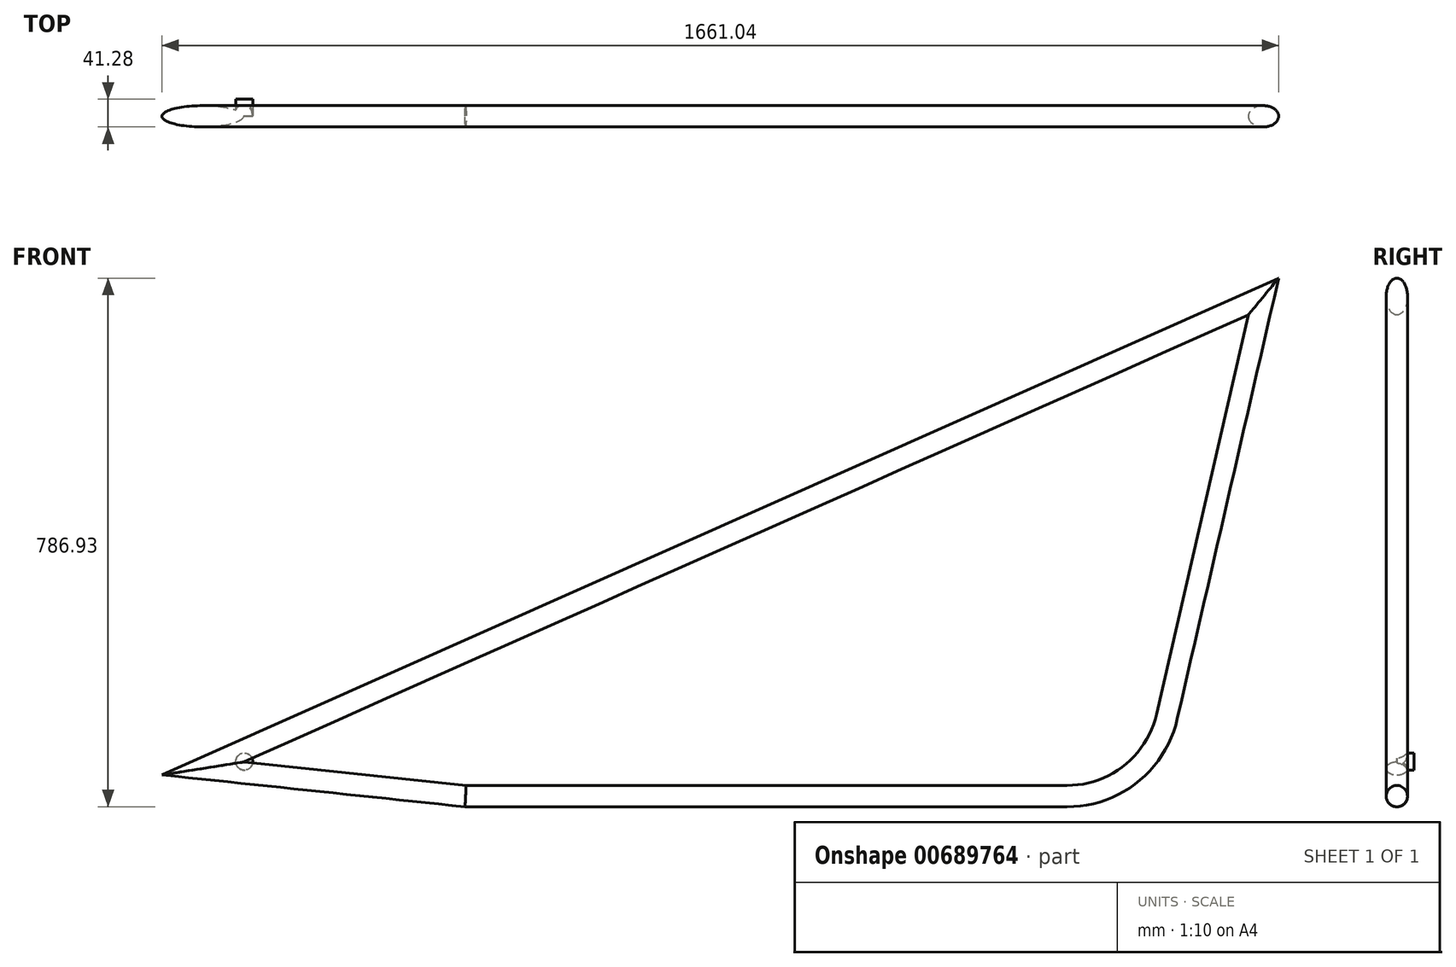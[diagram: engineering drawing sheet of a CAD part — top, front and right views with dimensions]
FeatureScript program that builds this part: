
annotation { "Feature Type Name" : "Feature", "Feature Type Description" : "" }
export const myFeature = defineFeature(function(context is Context, id is Id, definition is map)
    precondition{}
    {
        {
            var Q0;
            Q0=qCreatedBy(makeId("Front.planeOp"),FACE);
            var sketch = newSketch(context, id + "F0", { "sketchPlane" : qUnion([Q0])});
            skLineSegment(sketch, "E0", {"start": v(842.45, 702.52) * mm, "end": v(-735.42, 0) * mm});
            skLineSegment(sketch, "E1", {"start": v(-735.42, 0) * mm, "end": v(-344.34, -41.1) * mm});
            skLineSegment(sketch, "E2", {"start": v(-344.34, -41.1) * mm, "end": v(550.3, -41.1) * mm});
            skLineSegment(sketch, "E3", {"start": v(842.45, 702.52) * mm, "end": v(698.83, 77.18) * mm});
            skPoint(sketch, "E4.visualSharp", {"position": v(671.66, -41.1) * mm});
            skArc(sketch, "E4.filletArc", {"start": v(550.3, -41.1) * mm, "mid": v(645.23, -7.92) * mm, "end": v(698.83, 77.18) * mm});
            skLineSegment(sketch, "E5", {"start": v(-29.69, 314.21) * mm, "end": v(-29.69, -41.1) * mm});
            skLineSegment(sketch, "E6", {"start": v(-735.42, 0) * mm, "end": v(-539.88, -20.55) * mm});
            skLineSegment(sketch, "E7", {"start": v(-735.42, 0) * mm, "end": v(1316.3, 0) * mm});
            skLineSegment(sketch, "E8", {"start": v(842.45, 702.52) * mm, "end": v(842.45, -98.36) * mm});
            skLineSegment(sketch, "E9", {"start": v(842.45, 702.52) * mm, "end": v(1316.3, 0) * mm});
            skSolve(sketch);
        }
        {
            var Q0;
            Q0=qCreatedBy(makeId("Right.planeOp"),FACE);
            var sketch = newSketch(context, id + "F1", { "sketchPlane" : qUnion([Q0])});
            skCircle(sketch, "E10", {"center": v(0, -41.1) * mm, "radius": 15.88 * mm});
            skLineSegment(sketch, "E11", {"start": v(20.8, -41.41) * mm, "end": v(0, 154.77) * mm});
            skSolve(sketch);
        }
        {
            var Q0;
            Q0=makeQuery(id+"F1.imprint","IMPRINT",FACE,{"disambiguationData":[TD([[makeQuery(id+"F1.imprint","IMPRINT",EDGE,{"derivedFrom":sQuery(id+"F1.wireOp",EDGE,"E10")}),1.0]])]});
            var Q1;
            Q1=sQuery(id+"F0.wireOp",EDGE,"E2");
            var Q2;
            Q2=sQuery(id+"F0.wireOp",EDGE,"E4.filletArc");
            var Q3;
            Q3=sQuery(id+"F0.wireOp",EDGE,"E3");
            var Q4;
            Q4=sQuery(id+"F0.wireOp",EDGE,"E1");
            var Q5;
            Q5=sQuery(id+"F0.wireOp",EDGE,"E0");
            sweep(context, id + "F2", {"profiles" : qUnion([Q0]), "path" : qUnion([Q1, Q2, Q3, Q4, Q5])});
        }
        {
            var Q0;
            Q0=qCreatedBy(makeId("Front.planeOp"),FACE);
            var sketch = newSketch(context, id + "F3", { "sketchPlane" : qUnion([Q0])});
            skCircle(sketch, "E12", {"center": v(-673.59, 10.26) * mm, "radius": 12.7 * mm});
            skSolve(sketch);
        }
        {
            var Q0;
            Q0=makeQuery(id+"F3.imprint","IMPRINT",FACE,{"disambiguationData":[TD([[makeQuery(id+"F3.imprint","IMPRINT",EDGE,{"derivedFrom":sQuery(id+"F3.wireOp",EDGE,"E12")}),1.0]])]});
            extrude(context, id + "F4", {"entities" : qUnion([Q0]), "operationType" : NewBodyOperationType.ADD, "oppositeDirection" : true, "depth" : 25.4 * mm, "offsetDistance" : 25.4 * mm});
        }
    });
